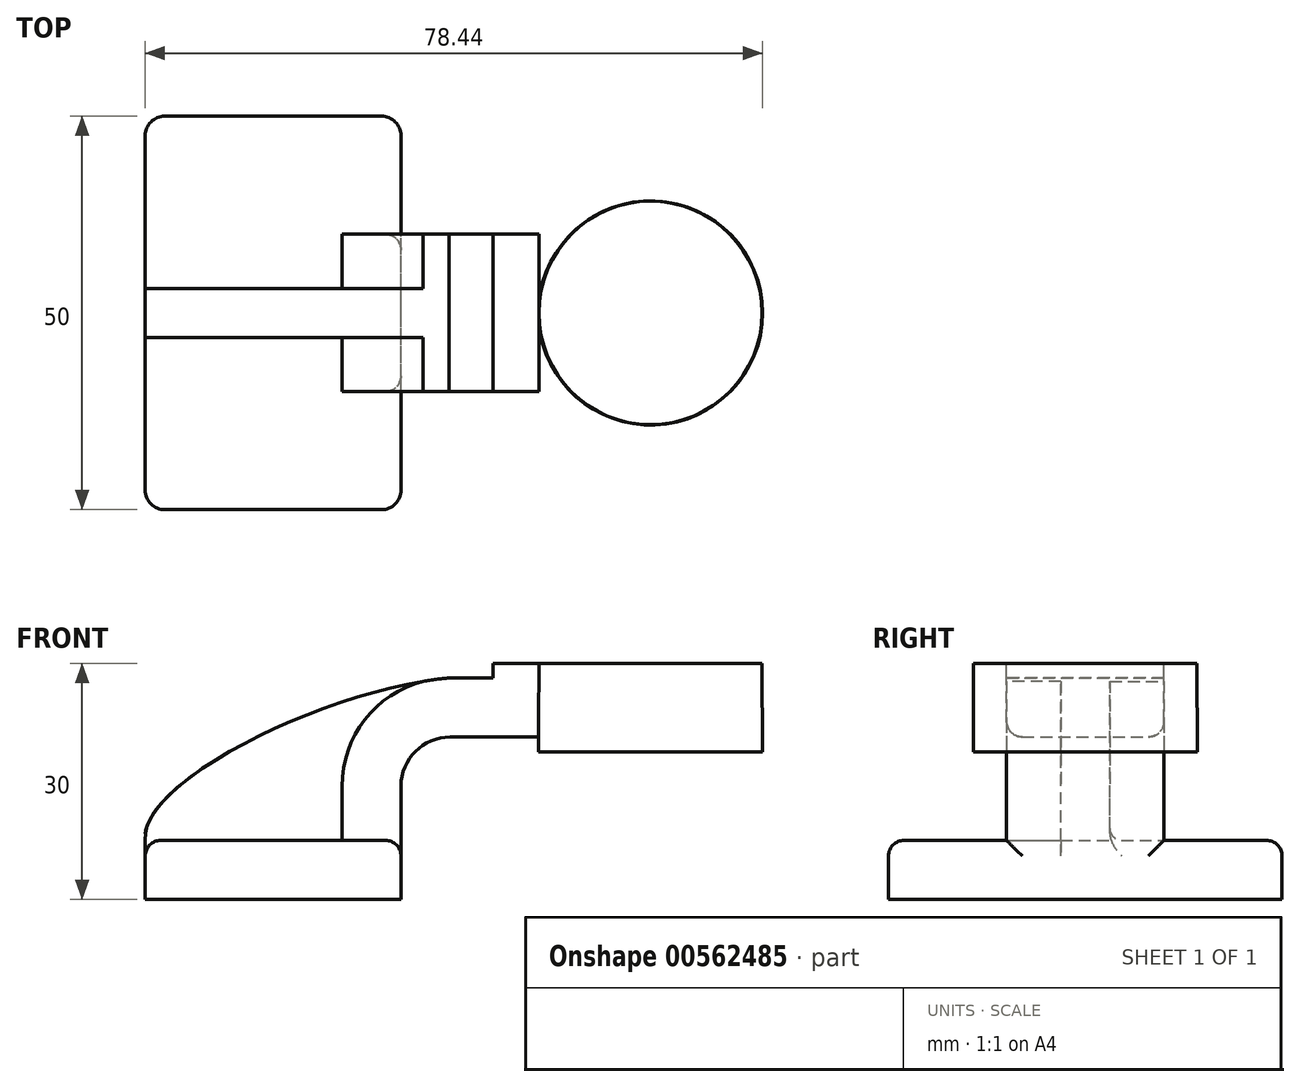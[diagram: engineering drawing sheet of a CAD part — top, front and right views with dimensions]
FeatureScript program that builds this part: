
annotation { "Feature Type Name" : "Feature", "Feature Type Description" : "" }
export const myFeature = defineFeature(function(context is Context, id is Id, definition is map)
    precondition{}
    {
        {
            var Q0;
            Q0=qCreatedBy(makeId("Front.planeOp"),FACE);
            var sketch = newSketch(context, id + "F0", { "sketchPlane" : qUnion([Q0])});
            skLineSegment(sketch, "E0.bottom", {"start": v(16.25, -3.75) * mm, "end": v(-16.25, -3.75) * mm});
            skLineSegment(sketch, "E0.top", {"start": v(16.25, 3.75) * mm, "end": v(-16.25, 3.75) * mm});
            skLineSegment(sketch, "E0.left", {"start": v(16.25, -3.75) * mm, "end": v(16.25, 3.75) * mm});
            skLineSegment(sketch, "E0.right", {"start": v(-16.25, -3.75) * mm, "end": v(-16.25, 3.75) * mm});
            skPoint(sketch, "E0.middle", {"position": v(0, 0) * mm});
            skLineSegment(sketch, "E1.bottom", {"start": v(47.94, 15) * mm, "end": v(27.94, 15) * mm});
            skLineSegment(sketch, "E1.top", {"start": v(47.94, 26.25) * mm, "end": v(27.94, 26.25) * mm});
            skLineSegment(sketch, "E1.left", {"start": v(47.94, 15) * mm, "end": v(47.94, 26.25) * mm});
            skLineSegment(sketch, "E1.right", {"start": v(27.94, 15) * mm, "end": v(27.94, 26.25) * mm});
            skPoint(sketch, "E1.middle", {"position": v(37.94, 20.63) * mm});
            skLineSegment(sketch, "E2", {"start": v(16.25, 3.75) * mm, "end": v(16.25, 10.63) * mm});
            skArc(sketch, "E3", {"start": v(16.25, 10.63) * mm, "mid": v(18.08, 15.05) * mm, "end": v(22.5, 16.88) * mm});
            skLineSegment(sketch, "E4", {"start": v(22.5, 16.88) * mm, "end": v(33.75, 16.88) * mm});
            skLineSegment(sketch, "E5.0", {"start": v(22.5, 24.38) * mm, "end": v(33.75, 24.38) * mm});
            skArc(sketch, "E5.1", {"start": v(8.75, 10.63) * mm, "mid": v(12.78, 20.35) * mm, "end": v(22.5, 24.38) * mm});
            skLineSegment(sketch, "E5.2", {"start": v(8.75, 3.75) * mm, "end": v(8.75, 10.63) * mm});
            skLineSegment(sketch, "E6", {"start": v(33.7, 15) * mm, "end": v(33.75, 26.25) * mm});
            skFitSpline(sketch, "E7", {"points": [v(-16.25, 3.75) * mm, v(27.94, 24.38) * mm], "startDerivative": vector(-2.7, 25.67) * mm, "endDerivative": vector(43, -5.09) * mm});
            skSolve(sketch);
        }
        {
            var Q0;
            Q0=makeQuery(id+"F0.imprint","IMPRINT",FACE,{"disambiguationData":[TD([[makeQuery(id+"F0.imprint","IMPRINT",EDGE,{"derivedFrom":sQuery(id+"F0.wireOp",EDGE,"E0.bottom")}),-1.0]])]});
            extrude(context, id + "F1", {"entities" : qUnion([Q0]), "endBound" : BoundingType.SYMMETRIC, "depth" : 50 * mm, "offsetDistance" : 25 * mm});
        }
        {
            var Q0;
            {var subQ1=sQuery(id+"F0.wireOp",EDGE,"E2");Q0=makeQuery(id+"F0.imprint","IMPRINT",FACE,{"disambiguationData":[TD([[makeQuery(id+"F0.imprint","IMPRINT",EDGE,{"derivedFrom":subQ1}),1.0]])]});}
            var Q1;
            {var subQ1=sQuery(id+"F0.wireOp",EDGE,"E1.right");var subQ3=sQuery(id+"F0.wireOp",EDGE,"E4");var subQ4=makeQuery(id+"F0.imprint","INTERSECT",VERTEX,{"derivedFrom":[subQ1,subQ3]});Q1=makeQuery(id+"F0.imprint","IMPRINT",FACE,{"disambiguationData":[TD([[makeQuery(id+"F0.imprint","IMPRINT",EDGE,{"disambiguationData":[TD([[subQ4,-1.0]])],"derivedFrom":subQ3}),1.0]])]});}
            var Q2;
            {var subQ0=sQuery(id+"F0.wireOp",EDGE,"E1.right");var subQ1=sQuery(id+"F0.wireOp",EDGE,"E1.top");var subQ2=makeQuery(id+"F0.imprint","INTERSECT",VERTEX,{"derivedFrom":[subQ1,subQ0]});Q2=makeQuery(id+"F0.imprint","IMPRINT",FACE,{"disambiguationData":[TD([[makeQuery(id+"F0.imprint","IMPRINT",EDGE,{"disambiguationData":[TD([[subQ2,1.0]])],"derivedFrom":subQ1}),1.0]])]});}
            extrude(context, id + "F2", {"entities" : qUnion([Q0, Q1, Q2]), "operationType" : NewBodyOperationType.ADD, "endBound" : BoundingType.SYMMETRIC, "depth" : 20 * mm, "offsetDistance" : 25 * mm});
        }
        {
            var Q0;
            {var subQ3=sQuery(id+"F0.wireOp",EDGE,"E5.2");Q0=makeQuery(id+"F0.imprint","IMPRINT",FACE,{"disambiguationData":[TD([[makeQuery(id+"F0.imprint","IMPRINT",EDGE,{"derivedFrom":subQ3}),1.0]])]});}
            extrude(context, id + "F3", {"entities" : qUnion([Q0]), "operationType" : NewBodyOperationType.ADD, "endBound" : BoundingType.SYMMETRIC, "depth" : 6.25 * mm, "offsetDistance" : 25 * mm});
        }
        {
            var Q0;
            {var subQ4=sQuery(id+"F0.wireOp",EDGE,"E1.left");Q0=makeQuery(id+"F0.imprint","IMPRINT",FACE,{"disambiguationData":[TD([[makeQuery(id+"F0.imprint","IMPRINT",EDGE,{"derivedFrom":subQ4}),1.0]])]});}
            var Q1;
            Q1=sQuery(id+"F0.wireOp",EDGE,"E1.left");
            revolve(context, id + "F4", {"operationType" : NewBodyOperationType.ADD, "entities" : qUnion([Q0]), "axis" : qUnion([Q1]), "revolveType" : RevolveType.FULL});
        }
        {
            var Q0;
            Q0=makeQuery(id+"F1.opExtrude","CAP_EDGE",EDGE,{"disambiguationData":[OSD([sQuery(id+"F0.wireOp",EDGE,"E0.right")])],"isStart":false});
            var Q1;
            Q1=makeQuery(id+"F1.opExtrude","CAP_EDGE",EDGE,{"disambiguationData":[OSD([sQuery(id+"F0.wireOp",EDGE,"E0.left")])],"isStart":false});
            var Q2;
            Q2=makeQuery(id+"F1.opExtrude","CAP_EDGE",EDGE,{"disambiguationData":[OSD([sQuery(id+"F0.wireOp",EDGE,"E0.right")])],"isStart":true});
            var Q3;
            Q3=makeQuery(id+"F1.opExtrude","CAP_EDGE",EDGE,{"disambiguationData":[OSD([sQuery(id+"F0.wireOp",EDGE,"E0.left")])],"isStart":true});
            fillet(context, id + "F5", {"entities" : qUnion([Q0, Q1, Q2, Q3]), "radius" : 2.5 * mm, "tangentPropagation" : true, "allowEdgeOverflow" : false});
        }
        {
            var Q0;
            {var subQ0=sQuery(id+"F0.wireOp",EDGE,"E5.1");Q0=makeQuery(id+"F2.opExtrude","CAP_EDGE",EDGE,{"disambiguationData":[OSD([subQ0]),TDD([makeQuery(id+"F0.imprint","IMPRINT",EDGE,{"disambiguationData":[TD([[makeQuery(id+"F0.imprint","INTERSECT",VERTEX,{"derivedFrom":[subQ0,sQuery(id+"F0.wireOp",EDGE,"E5.2")]}),-1.0]])],"derivedFrom":subQ0})])],"isStart":true});}
            var Q1;
            Q1=makeQuery(id+"F2.opExtrude","CAP_EDGE",EDGE,{"disambiguationData":[OSD([sQuery(id+"F0.wireOp",EDGE,"E2")])],"isStart":true});
            var Q2;
            Q2=makeQuery(id+"F1.opExtrude","CAP_EDGE",EDGE,{"disambiguationData":[OSD([sQuery(id+"F0.wireOp",EDGE,"E0.top")])],"isStart":true});
            var Q3;
            {var subQ0=sQuery(id+"F0.wireOp",EDGE,"E0.left");var subQ1=sQuery(id+"F0.wireOp",EDGE,"E2");var subQ2=sQuery(id+"F0.wireOp",EDGE,"E0.top");Q3=makeQuery(id+"F2.boolean.opBoolean","SPLIT",EDGE,{"disambiguationData":[TD([makeQuery(id+"F1.opExtrude","CAP_FACE",FACE,{"disambiguationData":[OSD([sQuery(id+"F0.wireOp",EDGE,"E0.bottom"),subQ2,subQ0,sQuery(id+"F0.wireOp",EDGE,"E0.right")])],"isStart":false})])],"derivedFrom":makeQuery(id+"F1.opExtrude","SWEPT_EDGE",EDGE,{"disambiguationData":[OSD([subQ2,subQ0,subQ1])]})});}
            var Q4;
            Q4=makeQuery(id+"F2.opExtrude","CAP_EDGE",EDGE,{"disambiguationData":[OSD([sQuery(id+"F0.wireOp",EDGE,"E4")])],"isStart":false});
            var Q5;
            {var subQ0=sQuery(id+"F0.wireOp",EDGE,"E5.1");Q5=makeQuery(id+"F2.opExtrude","CAP_EDGE",EDGE,{"disambiguationData":[OSD([subQ0]),TDD([makeQuery(id+"F0.imprint","IMPRINT",EDGE,{"disambiguationData":[TD([[makeQuery(id+"F0.imprint","INTERSECT",VERTEX,{"derivedFrom":[subQ0,sQuery(id+"F0.wireOp",EDGE,"E5.2")]}),-1.0]])],"derivedFrom":subQ0})])],"isStart":false});}
            fillet(context, id + "F6", {"entities" : qUnion([Q0, Q1, Q2, Q3, Q4, Q5]), "radius" : 2 * mm, "tangentPropagation" : true, "allowEdgeOverflow" : false});
        }
        {
            var Q0;
            Q0=makeQuery(id+"F3.opExtrude","CAP_EDGE",EDGE,{"disambiguationData":[OSD([sQuery(id+"F0.wireOp",EDGE,"E0.top")])],"isStart":false});
            var Q1;
            Q1=makeQuery(id+"F2.opExtrude","CAP_EDGE",EDGE,{"disambiguationData":[OSD([sQuery(id+"F0.wireOp",EDGE,"E0.top")])],"isStart":false});
            var Q2;
            Q2=makeQuery(id+"F2.opExtrude","CAP_EDGE",EDGE,{"disambiguationData":[OSD([sQuery(id+"F0.wireOp",EDGE,"E0.top")])],"isStart":true});
            var Q3;
            Q3=makeQuery(id+"F3.opExtrude","CAP_EDGE",EDGE,{"disambiguationData":[OSD([sQuery(id+"F0.wireOp",EDGE,"E0.top")])],"isStart":true});
            fillet(context, id + "F7", {"entities" : qUnion([Q0, Q1, Q2, Q3]), "radius" : 1.5 * mm, "tangentPropagation" : true, "allowEdgeOverflow" : false});
        }
    });
